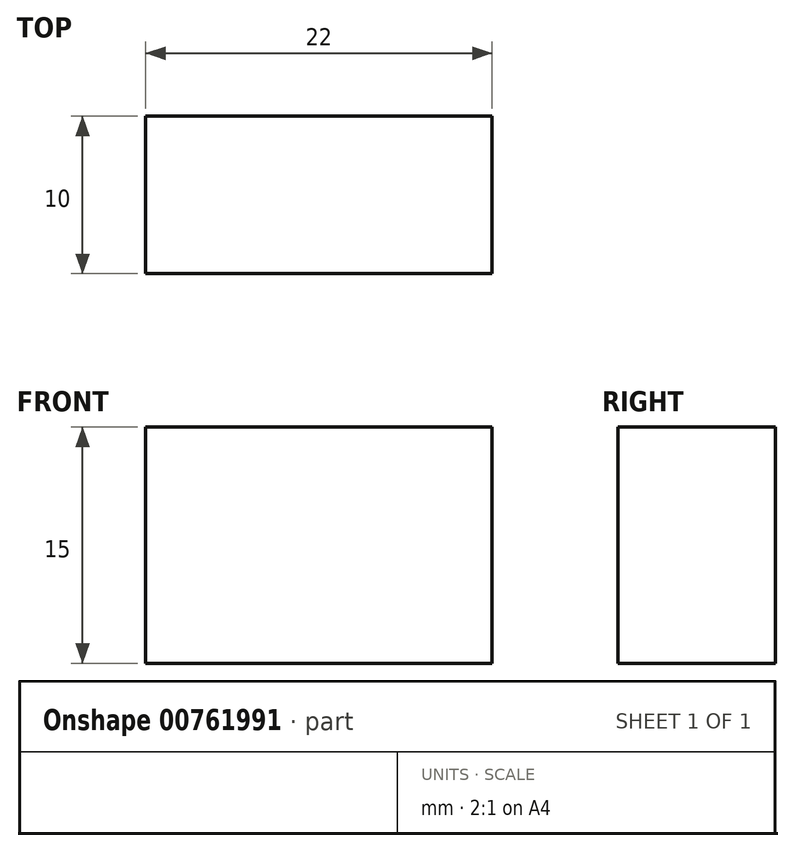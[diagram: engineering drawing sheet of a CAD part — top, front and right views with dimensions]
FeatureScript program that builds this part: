
annotation { "Feature Type Name" : "Feature", "Feature Type Description" : "" }
export const myFeature = defineFeature(function(context is Context, id is Id, definition is map)
    precondition{}
    {
        {
            var Q0;
            Q0=qCreatedBy(makeId("Front.planeOp"),FACE);
            var sketch = newSketch(context, id + "F0", { "sketchPlane" : qUnion([Q0])});
            skLineSegment(sketch, "E0.bottom", {"start": v(-26.98, -4.98) * mm, "end": v(-4.98, -4.98) * mm});
            skLineSegment(sketch, "E0.top", {"start": v(-26.98, -19.98) * mm, "end": v(-4.98, -19.98) * mm});
            skLineSegment(sketch, "E0.left", {"start": v(-26.98, -4.98) * mm, "end": v(-26.98, -19.98) * mm});
            skLineSegment(sketch, "E0.right", {"start": v(-4.98, -4.98) * mm, "end": v(-4.98, -19.98) * mm});
            skSolve(sketch);
        }
        {
            var Q0;
            Q0=makeQuery(id+"F0.imprint","IMPRINT",FACE,{"disambiguationData":[TD([[makeQuery(id+"F0.imprint","IMPRINT",EDGE,{"derivedFrom":sQuery(id+"F0.wireOp",EDGE,"E0.bottom")}),-1.0]])]});
            extrude(context, id + "F1", {"entities" : qUnion([Q0]), "depth" : 10 * mm, "offsetDistance" : 25.4 * mm});
        }
    });
